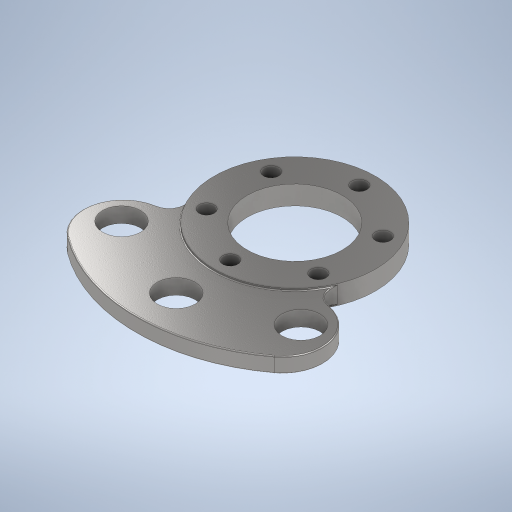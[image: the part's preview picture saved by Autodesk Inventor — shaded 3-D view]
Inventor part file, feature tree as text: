
AUTODESK INVENTOR PART (.ipt)
format: ipt  version: 2024 (Build 280153000, 153)  size: 392,192 bytes
history: native  units: mm
features: sketch x3, extrude x2, hole x2, fillet x2, pattern_circular x1
ambient origin geometry x8: Origin, YZ Plane, XZ Plane, XY Plane, X Axis, Y Axis, Z Axis, Center Point
bodies: Volumenkörper1 (feature_tree)
feature tree (10):
  sketch  "Skizze1"  dims[d0=85.0mm d1=50.0mm]
  extrude  "Extrusion1"  Depth=50.0mm
  extrude  "Extrusion2"  Depth=8.0mm
  hole  "Bohrung1"  [1 undecoded]
  pattern_circular  "Runde Anordnung1"  [2 undecoded]
  hole  "Bohrung2"  [1 undecoded]
  fillet  "Rundung1"  [1 undecoded]
  fillet  "Rundung2"  [1 undecoded]
  sketch  "Skizze2"  dims[d2=21.0mm d3=8.0mm]
  sketch  "Skizze3"  dims[d4=84.0mm d5=93.0mm d6=10.0mm d7=0.0mm d8=8.0mm d9=0.0mm d10=90.0deg d11=45.0deg d12=68.0mm d13=30.0deg d14=8.0mm d15=6.0mm d16=4.0mm d17=2.0mm d18=90.0deg d19=8.0mm d20=20.594885mm d21=60.0mm d22=360.0deg d24=70.0mm d25=20.0mm d26=6.0mm d27=4.0mm d28=2.0mm d29=90.0deg d30=8.0mm d31=20.594885mm d32=0.5mm d33=0.5mm d34=91.0mm d35=44.0mm d36=44.0mm]
note: 6 required parameter values undecoded (feature->parameter linkage not recoverable at this tier; creation-order binding heuristic only, values carry confidence <= 0.55)
